# Revit family: Reece_Sink_Memo_Hugo_Inset or Undermount_Double Bowl_No Drainer
name_source: partatom
category: Plumbing Fixtures
revit_build: Autodesk Revit 2018 (Build: 20190510_1515(x64)
units: mm (PartAtom-declared; Revit-internal decimal feet)

## family parameters
Cut with Voids When Loaded = No
Host = Face
Part Type = Normal
Room Calculation Point = Yes
Round Connector Dimension = Use Diameter
Shared = Yes

## types (1)
- 0 Taphole_Stainless Steel
    CWFU = 0
    Default Elevation = 0 mm  [stored 0 ft]
    Description = Memo Hugo Double Bowl Sink No Taphole Stainless Steel
    Disclaimer = THIS FILE IS THE PROPERTY OF THE REECE GROUP. IT MAY NOT BE REPRODUCED, REVERSE-ENGINEERED OR MODIFIED. ANY REPUBLICATION, TRANSMISSION OR DISTRIBUTION FOR THE PURPOSE OF COMMERCIALLY EXPLOITING THE FILES IS PROHIBITED.
    HWFU = 0
    Keynote = Product #2402706, Reece_Sink_Memo_Hugo_Inset or Undermount_Double Bowl_No Drainer - 0 Taphole_Stainless Steel
    Manufacturer = Memo
    Model = Hugo
    Reece_Detail_Additional = No Overflow
    Reece_Detail_Connector = No Taphole
    Reece_Detail_Disclaimer = THIS FILE IS THE PROPERTY OF THE REECE GROUP. IT MAY NOT BE REPRODUCED, REVERSE-ENGINEERED OR MODIFIED. ANY REPUBLICATION, TRANSMISSION OR DISTRIBUTION FOR THE PURPOSE OF COMMERCIALLY EXPLOITING THE FILES IS PROHIBITED.
    Reece_Detail_Shape = No Drainer
    Reece_Material_Main = Reece_Metal_Stainless Steel_Satin
    Reece_Material_Secondary = Reece_Metal_Stainless Steel_Satin
    Reece_Overall_Capacity = 66.8 L
    Reece_Overall_Depth = 446 mm  [stored 1.46325 ft]
    Reece_Overall_Height = 220 mm  [stored 0.721785 ft]
    Reece_Overall_Width = 831 mm  [stored 2.72638 ft]
    Reece_Product_Brand = Memo
    Reece_Product_Description = Memo Hugo Double Bowl Sink No Taphole Stainless Steel
    Reece_Product_Mount = Inset / Undermount
    Reece_Product_Number = 2402706
    Reece_Product_Sub Brand = Hugo
    Reece_Product_Type = Sink
    Reece_Product_Web Page = https://www.reece.com.au
    Reece_Sink_Lip Thickness = 5 mm  [stored 0.0164042 ft]
    Reece_Sink_Opening = 23 mm
    Reece_Sink_Outlet = 40 mm  [stored 0.131234 ft]
    Reece_Sink_Outlet Offset = 50 mm
    Reece_Sink_Type = 0 Taphole_Stainless Steel
    Type Comments = Sink
    URL = https://www.reece.com.au
    WFU = 0

note: [stored X ft] marks values corroborated as IEEE doubles in the binary element streams (Revit-internal decimal feet)

## geometry (parser evidence)
native form markers: Sweep x7
no freeform markers — native parametric forms only
